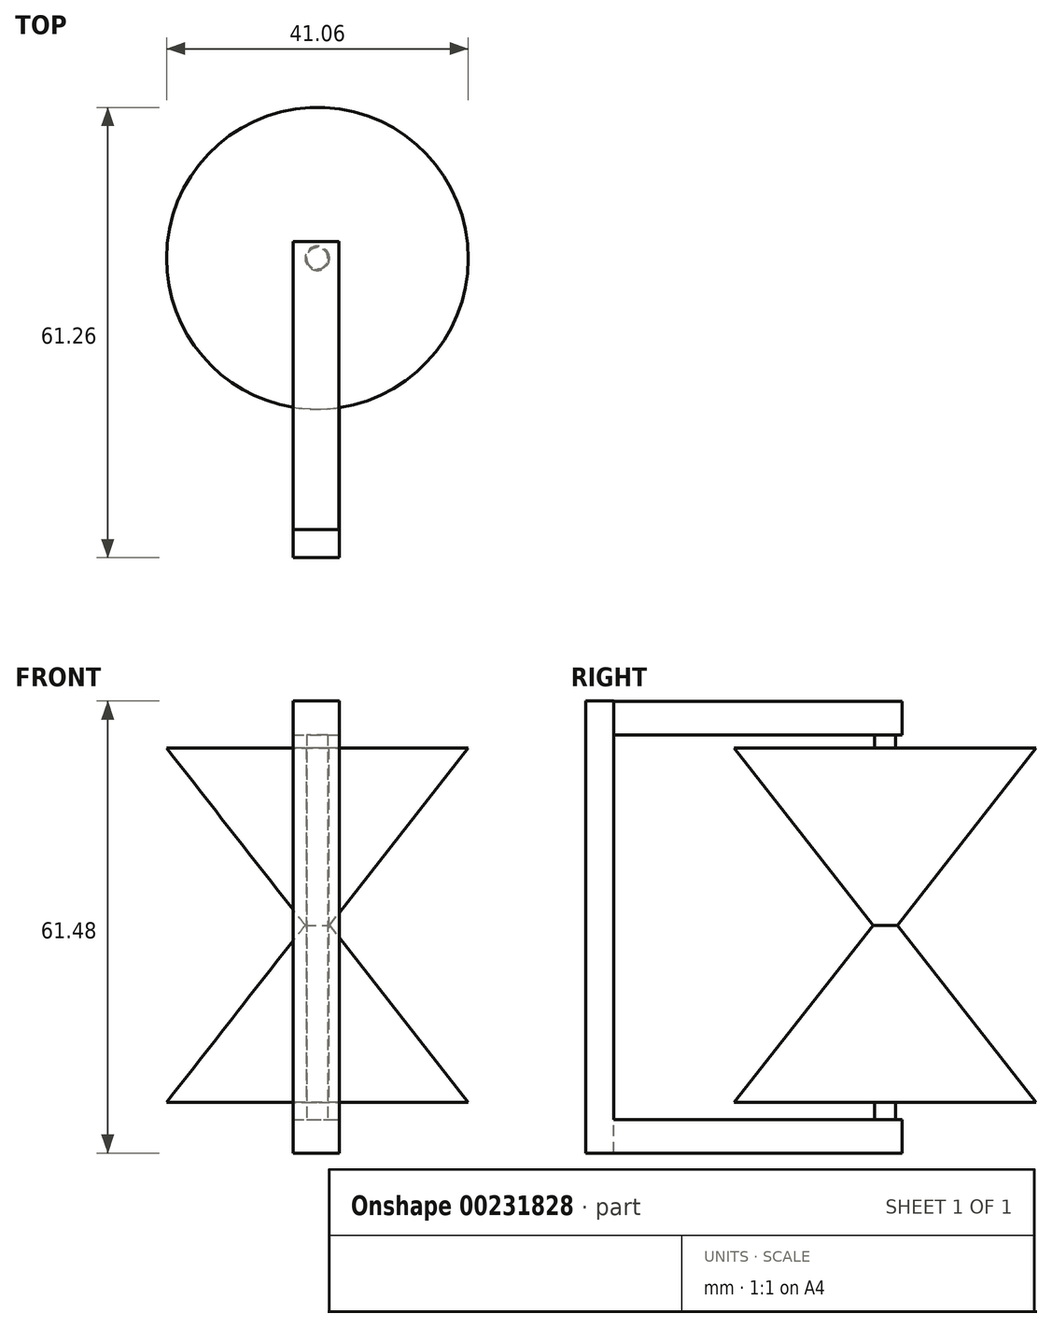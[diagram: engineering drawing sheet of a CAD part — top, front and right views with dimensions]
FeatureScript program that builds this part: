
annotation { "Feature Type Name" : "Feature", "Feature Type Description" : "" }
export const myFeature = defineFeature(function(context is Context, id is Id, definition is map)
    precondition{}
    {
        {
            var Q0;
            Q0=qCreatedBy(makeId("Front.planeOp"),FACE);
            var sketch = newSketch(context, id + "F0", { "sketchPlane" : qUnion([Q0])});
            skLineSegment(sketch, "E0", {"start": v(0, 0) * mm, "end": v(-18.88, 24.1) * mm});
            skLineSegment(sketch, "E1", {"start": v(-18.88, 24.1) * mm, "end": v(1.65, 24.1) * mm});
            skLineSegment(sketch, "E2", {"start": v(1.65, 24.1) * mm, "end": v(1.65, 0) * mm});
            skLineSegment(sketch, "E3.MirrorCS", {"start": v(1.65, -24.1) * mm, "end": v(1.65, 0) * mm});
            skLineSegment(sketch, "E4.MirrorCS", {"start": v(0, 0) * mm, "end": v(-18.88, -24.1) * mm});
            skLineSegment(sketch, "E5.MirrorCS", {"start": v(-18.88, -24.1) * mm, "end": v(1.65, -24.1) * mm});
            skSolve(sketch);
        }
        {
            var Q0;
            Q0 = qSketchRegion(id + "F0", true);
            var Q1;
            Q1=sQuery(id+"F0.wireOp",EDGE,"E3.MirrorCS");
            revolve(context, id + "F1", {"entities" : qUnion([Q0]), "axis" : qUnion([Q1]), "revolveType" : RevolveType.FULL});
        }
        {
            var Q0;
            Q0=makeQuery(id+"F1.opRevolve","SWEPT_FACE",FACE,{"disambiguationData":[OSD([sQuery(id+"F0.wireOp",EDGE,"E5.MirrorCS")])]});
            var sketch = newSketch(context, id + "F2", { "sketchPlane" : qUnion([Q0])});
            skCircle(sketch, "E6", {"center": v(1.65, 0) * mm, "radius": 1.55 * mm});
            skSolve(sketch);
        }
        {
            var Q0;
            Q0 = qSketchRegion(id + "F2", true);
            extrude(context, id + "F3", {"entities" : qUnion([Q0]), "operationType" : NewBodyOperationType.REMOVE, "oppositeDirection" : true, "depth" : 70.61 * mm});
        }
        {
            var Q0;
            Q0=qCreatedBy(makeId("Top.planeOp"),FACE);
            var sketch = newSketch(context, id + "F4", { "sketchPlane" : qUnion([Q0])});
            skCircle(sketch, "E7", {"center": v(1.64, 0) * mm, "radius": 1.44 * mm});
            skSolve(sketch);
        }
        {
            var Q0;
            Q0 = qSketchRegion(id + "F4", true);
            extrude(context, id + "F5", {"entities" : qUnion([Q0]), "depth" : 26.67 * mm, "hasSecondDirection" : true, "secondDirectionOppositeDirection" : true, "secondDirectionDepth" : 27.18 * mm});
        }
        {
            var Q0;
            Q0=makeQuery(id+"F5.opExtrude","CAP_FACE",FACE,{"disambiguationData":[OSD([sQuery(id+"F4.wireOp",EDGE,"E7")])],"isStart":false});
            var sketch = newSketch(context, id + "F6", { "sketchPlane" : qUnion([Q0])});
            skLineSegment(sketch, "E8.bottom", {"start": v(-1.65, 2.3) * mm, "end": v(4.58, 2.3) * mm});
            skLineSegment(sketch, "E8.top", {"start": v(-1.65, -36.93) * mm, "end": v(4.58, -36.93) * mm});
            skLineSegment(sketch, "E8.left", {"start": v(-1.65, 2.3) * mm, "end": v(-1.65, -36.93) * mm});
            skLineSegment(sketch, "E8.right", {"start": v(4.58, 2.3) * mm, "end": v(4.58, -36.93) * mm});
            skSolve(sketch);
        }
        {
            var Q0;
            Q0 = qSketchRegion(id + "F6", true);
            extrude(context, id + "F7", {"entities" : qUnion([Q0]), "operationType" : NewBodyOperationType.ADD, "depth" : 3.8 * mm, "hasSecondDirection" : true, "secondDirectionOppositeDirection" : true, "secondDirectionDepth" : 0.76 * mm});
        }
        {
            var Q0;
            Q0=makeQuery(id+"F5.opExtrude","CAP_FACE",FACE,{"disambiguationData":[OSD([sQuery(id+"F4.wireOp",EDGE,"E7")])],"isStart":true});
            var sketch = newSketch(context, id + "F8", { "sketchPlane" : qUnion([Q0])});
            skLineSegment(sketch, "E9.bottom", {"start": v(-1.67, -2.33) * mm, "end": v(4.61, -2.33) * mm});
            skLineSegment(sketch, "E9.top", {"start": v(-1.67, 36.92) * mm, "end": v(4.61, 36.92) * mm});
            skLineSegment(sketch, "E9.left", {"start": v(-1.67, -2.33) * mm, "end": v(-1.67, 36.92) * mm});
            skLineSegment(sketch, "E9.right", {"start": v(4.61, -2.33) * mm, "end": v(4.61, 36.92) * mm});
            skSolve(sketch);
        }
        {
            var Q0;
            Q0 = qSketchRegion(id + "F8", true);
            extrude(context, id + "F9", {"entities" : qUnion([Q0]), "operationType" : NewBodyOperationType.ADD, "depth" : 3.8 * mm, "hasSecondDirection" : true, "secondDirectionOppositeDirection" : true, "secondDirectionDepth" : 0.76 * mm});
        }
        {
            var Q0;
            Q0=makeQuery(id+"F9.opExtrude","SWEPT_FACE",FACE,{"disambiguationData":[OSD([sQuery(id+"F8.wireOp",EDGE,"E9.top")])]});
            var sketch = newSketch(context, id + "F10", { "sketchPlane" : qUnion([Q0])});
            skLineSegment(sketch, "E10.bottom", {"start": v(-1.66, 30.5) * mm, "end": v(4.61, 30.5) * mm});
            skLineSegment(sketch, "E10.top", {"start": v(-1.66, -30.99) * mm, "end": v(4.61, -30.99) * mm});
            skLineSegment(sketch, "E10.left", {"start": v(-1.66, 30.5) * mm, "end": v(-1.66, -30.99) * mm});
            skLineSegment(sketch, "E10.right", {"start": v(4.61, 30.5) * mm, "end": v(4.61, -30.99) * mm});
            skSolve(sketch);
        }
        {
            var Q0;
            Q0 = qSketchRegion(id + "F10", true);
            extrude(context, id + "F11", {"entities" : qUnion([Q0]), "operationType" : NewBodyOperationType.ADD, "depth" : 3.8 * mm});
        }
    });
